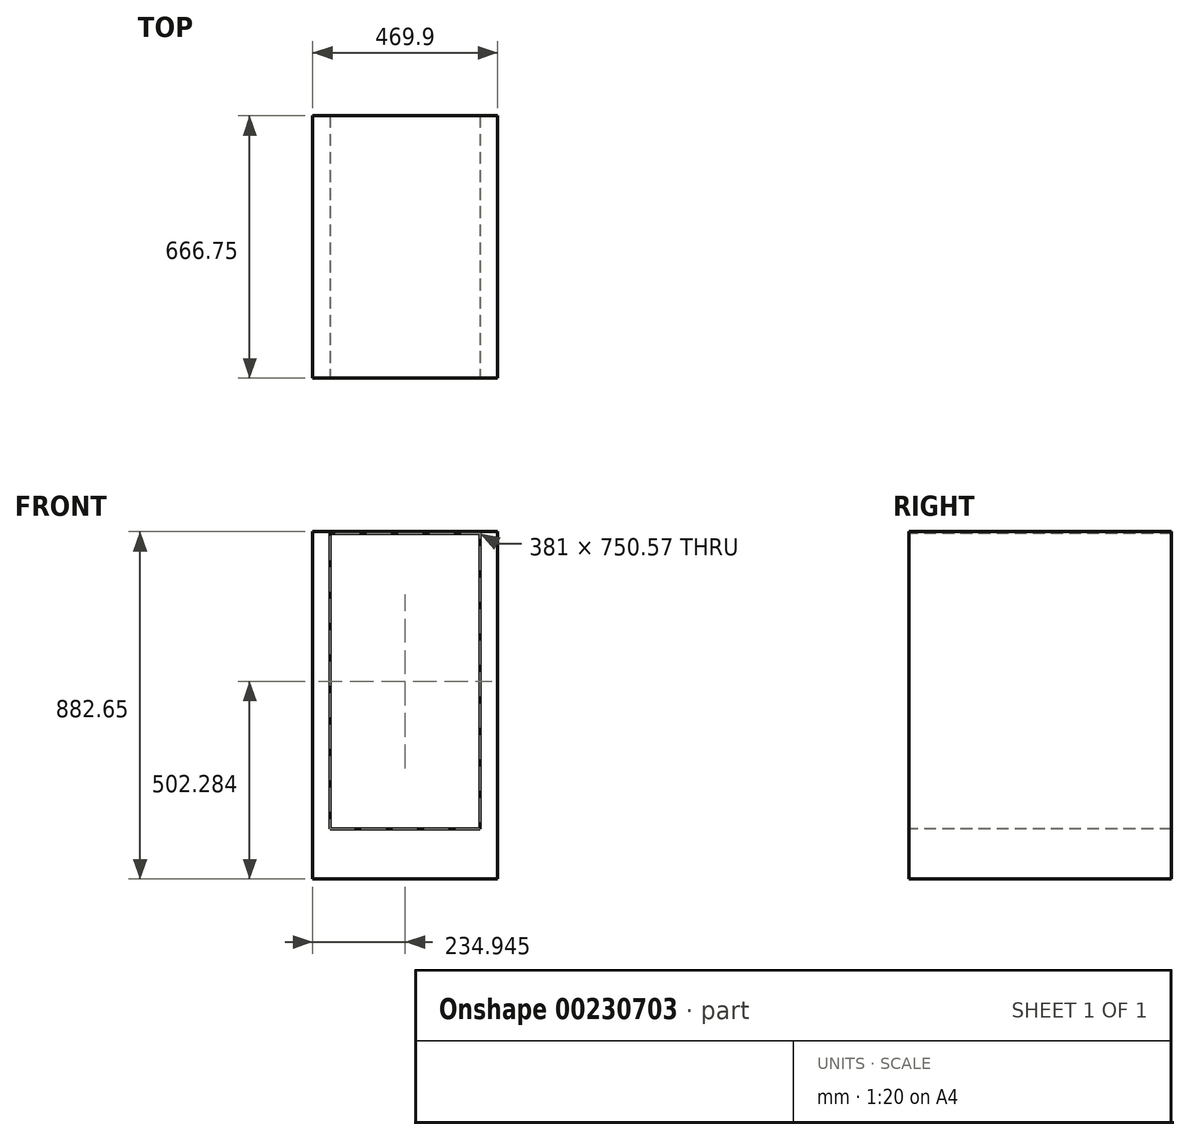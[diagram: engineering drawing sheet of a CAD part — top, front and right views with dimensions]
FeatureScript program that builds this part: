
annotation { "Feature Type Name" : "Feature", "Feature Type Description" : "" }
export const myFeature = defineFeature(function(context is Context, id is Id, definition is map)
    precondition{}
    {
        {
            var Q0;
            Q0=qCreatedBy(makeId("Front.planeOp"),FACE);
            var sketch = newSketch(context, id + "F0", { "sketchPlane" : qUnion([Q0])});
            skLineSegment(sketch, "E0.bottom", {"start": v(-518.24, 434.34) * mm, "end": v(-137.24, 434.34) * mm});
            skLineSegment(sketch, "E0.top", {"start": v(-518.24, 429.26) * mm, "end": v(-137.24, 429.26) * mm});
            skLineSegment(sketch, "E0.left", {"start": v(-518.24, 434.34) * mm, "end": v(-518.24, 429.26) * mm});
            skLineSegment(sketch, "E0.right", {"start": v(-137.24, 434.34) * mm, "end": v(-137.24, 429.26) * mm});
            skLineSegment(sketch, "E1.bottom", {"start": v(-518.24, 434.34) * mm, "end": v(-562.7, 434.34) * mm});
            skLineSegment(sketch, "E1.top", {"start": v(-518.24, -448.31) * mm, "end": v(-562.7, -448.31) * mm});
            skLineSegment(sketch, "E1.left", {"start": v(-518.24, 434.34) * mm, "end": v(-518.24, -448.31) * mm});
            skLineSegment(sketch, "E1.right", {"start": v(-562.7, 434.34) * mm, "end": v(-562.7, -448.31) * mm});
            skLineSegment(sketch, "E2.bottom", {"start": v(-137.24, 434.34) * mm, "end": v(-92.8, 434.34) * mm});
            skLineSegment(sketch, "E2.top", {"start": v(-137.24, -448.31) * mm, "end": v(-92.8, -448.31) * mm});
            skLineSegment(sketch, "E2.left", {"start": v(-137.24, 434.34) * mm, "end": v(-137.24, -448.31) * mm});
            skLineSegment(sketch, "E2.right", {"start": v(-92.8, 434.34) * mm, "end": v(-92.8, -448.31) * mm});
            skLineSegment(sketch, "E3.bottom", {"start": v(-518.24, -448.31) * mm, "end": v(-137.24, -448.31) * mm});
            skLineSegment(sketch, "E3.top", {"start": v(-518.24, -321.31) * mm, "end": v(-137.24, -321.31) * mm});
            skLineSegment(sketch, "E3.left", {"start": v(-518.24, -448.31) * mm, "end": v(-518.24, -321.31) * mm});
            skLineSegment(sketch, "E3.right", {"start": v(-137.24, -448.31) * mm, "end": v(-137.24, -321.31) * mm});
            skSolve(sketch);
        }
        {
            var Q0;
            {var subQ3=sQuery(id+"F0.wireOp",EDGE,"E1.bottom");Q0=makeQuery(id+"F0.imprint","IMPRINT",FACE,{"disambiguationData":[TD([[makeQuery(id+"F0.imprint","IMPRINT",EDGE,{"derivedFrom":subQ3}),1.0]])]});}
            var Q1;
            Q1=makeQuery(id+"F0.imprint","IMPRINT",FACE,{"disambiguationData":[TD([[makeQuery(id+"F0.imprint","IMPRINT",EDGE,{"derivedFrom":sQuery(id+"F0.wireOp",EDGE,"E3.bottom")}),1.0]])]});
            var Q2;
            {var subQ3=sQuery(id+"F0.wireOp",EDGE,"E2.bottom");Q2=makeQuery(id+"F0.imprint","IMPRINT",FACE,{"disambiguationData":[TD([[makeQuery(id+"F0.imprint","IMPRINT",EDGE,{"derivedFrom":subQ3}),-1.0]])]});}
            var Q3;
            {var subQ0=sQuery(id+"F0.wireOp",EDGE,"E0.bottom");Q3=makeQuery(id+"F0.imprint","IMPRINT",FACE,{"disambiguationData":[TD([[makeQuery(id+"F0.imprint","IMPRINT",EDGE,{"derivedFrom":subQ0}),-1.0]])]});}
            extrude(context, id + "F1", {"entities" : qUnion([Q0, Q1, Q2, Q3]), "oppositeDirection" : true, "depth" : 666.75 * mm});
        }
    });
